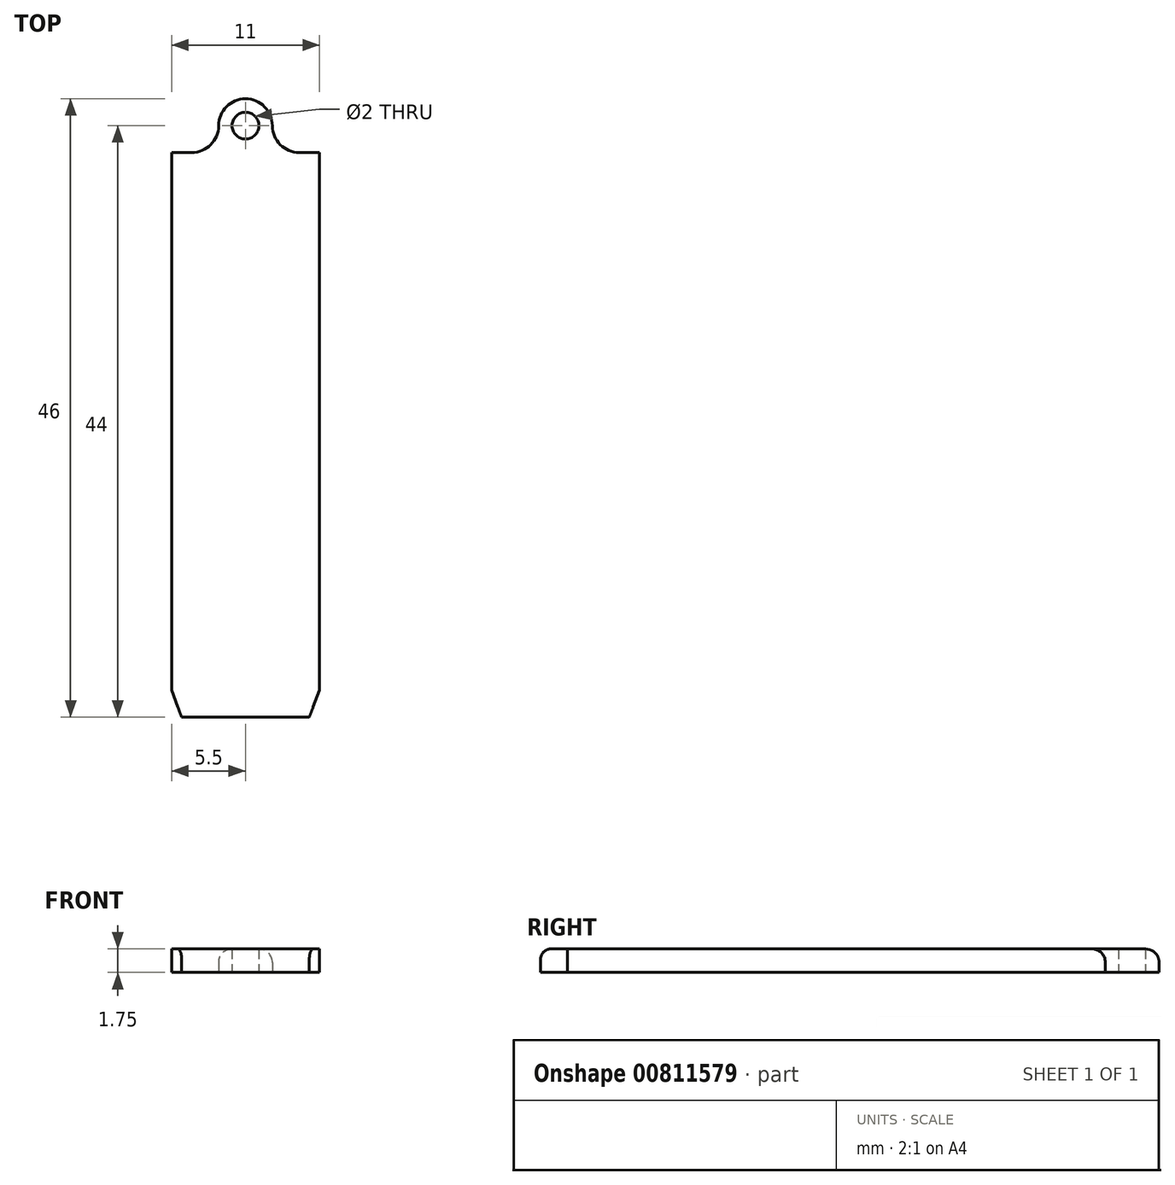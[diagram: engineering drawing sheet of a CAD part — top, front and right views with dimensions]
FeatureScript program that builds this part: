
annotation { "Feature Type Name" : "Feature", "Feature Type Description" : "" }
export const myFeature = defineFeature(function(context is Context, id is Id, definition is map)
    precondition{}
    {
        {
            var Q0;
            Q0=qCreatedBy(makeId("Top.planeOp"),FACE);
            var sketch = newSketch(context, id + "F0", { "sketchPlane" : qUnion([Q0])});
            skLineSegment(sketch, "E0.top", {"start": v(5.5, -21) * mm, "end": v(-5.5, -21) * mm});
            skLineSegment(sketch, "E0.left", {"start": v(5.5, 21) * mm, "end": v(5.5, -21) * mm});
            skLineSegment(sketch, "E0.right", {"start": v(-5.5, 21) * mm, "end": v(-5.5, -21) * mm});
            skPoint(sketch, "E0.middle", {"position": v(0, 0) * mm});
            skLineSegment(sketch, "E1", {"start": v(-2, 23) * mm, "end": v(-2, 23) * mm});
            skLineSegment(sketch, "E2", {"start": v(0, 25) * mm, "end": v(0, 25) * mm});
            skLineSegment(sketch, "E3", {"start": v(2, 23) * mm, "end": v(2, 23) * mm});
            skCircle(sketch, "E4", {"center": v(0, 23) * mm, "radius": 1 * mm});
            skPoint(sketch, "E4.centerSnap0", {"position": v(0, 25) * mm});
            skPoint(sketch, "E4.centerSnap1", {"position": v(-2, 23) * mm});
            skPoint(sketch, "E5.visualSharp", {"position": v(-2, 25) * mm});
            skArc(sketch, "E5.filletArc", {"start": v(0, 25) * mm, "mid": v(-1.41, 24.41) * mm, "end": v(-2, 23) * mm});
            skPoint(sketch, "E6.visualSharp", {"position": v(2, 25) * mm});
            skArc(sketch, "E6.filletArc", {"start": v(2, 23) * mm, "mid": v(1.41, 24.41) * mm, "end": v(0, 25) * mm});
            skLineSegment(sketch, "E7", {"start": v(-5.5, 21) * mm, "end": v(-4, 21) * mm});
            skLineSegment(sketch, "E8", {"start": v(4, 21) * mm, "end": v(5.5, 21) * mm});
            skPoint(sketch, "E9.visualSharp", {"position": v(-2, 21) * mm});
            skArc(sketch, "E9.filletArc", {"start": v(-4, 21) * mm, "mid": v(-2.59, 21.59) * mm, "end": v(-2, 23) * mm});
            skPoint(sketch, "E10.visualSharp", {"position": v(2, 21) * mm});
            skArc(sketch, "E10.filletArc", {"start": v(2, 23) * mm, "mid": v(2.59, 21.59) * mm, "end": v(4, 21) * mm});
            skSolve(sketch);
        }
        {
            var Q0;
            Q0 = qSketchRegion(id + "F0", true);
            extrude(context, id + "F1", {"entities" : qUnion([Q0]), "depth" : 1.75 * mm, "offsetDistance" : 25 * mm});
        }
        {
            var Q0;
            Q0=makeQuery(id+"F1.opExtrude","CAP_EDGE",EDGE,{"disambiguationData":[OSD([sQuery(id+"F0.wireOp",EDGE,"E9.filletArc")])],"isStart":false});
            fillet(context, id + "F2", {"entities" : qUnion([Q0]), "radius" : 1 * mm, "tangentPropagation" : true, "allowEdgeOverflow" : false});
        }
        {
            var Q0;
            Q0=makeQuery(id+"F1.opExtrude","CAP_FACE",FACE,{"disambiguationData":[OSD([sQuery(id+"F0.wireOp",EDGE,"E0.top"),sQuery(id+"F0.wireOp",EDGE,"E0.left"),sQuery(id+"F0.wireOp",EDGE,"E0.right"),sQuery(id+"F0.wireOp",EDGE,"E4"),sQuery(id+"F0.wireOp",EDGE,"E5.filletArc"),sQuery(id+"F0.wireOp",EDGE,"E6.filletArc"),sQuery(id+"F0.wireOp",EDGE,"E7"),sQuery(id+"F0.wireOp",EDGE,"E8"),sQuery(id+"F0.wireOp",EDGE,"E9.filletArc"),sQuery(id+"F0.wireOp",EDGE,"E10.filletArc")])],"isStart":false});
            var sketch = newSketch(context, id + "F3", { "sketchPlane" : qUnion([Q0])});
            skLineSegment(sketch, "E11", {"start": v(-4.75, -21) * mm, "end": v(-5.5, -19) * mm});
            skLineSegment(sketch, "E12", {"start": v(5.5, -19) * mm, "end": v(4.75, -21) * mm});
            skSolve(sketch);
        }
        {
            var Q0;
            {var subQ0=sQuery(id+"F3.wireOp",EDGE,"E11");Q0=makeQuery(id+"F3.imprint","IMPRINT",FACE,{"disambiguationData":[TD([[makeQuery(id+"F3.imprint","IMPRINT",EDGE,{"derivedFrom":subQ0}),1.0]])]});}
            var Q1;
            {var subQ0=sQuery(id+"F3.wireOp",EDGE,"E12");Q1=makeQuery(id+"F3.imprint","IMPRINT",FACE,{"disambiguationData":[TD([[makeQuery(id+"F3.imprint","IMPRINT",EDGE,{"derivedFrom":subQ0}),1.0]])]});}
            extrude(context, id + "F4", {"entities" : qUnion([Q0, Q1]), "operationType" : NewBodyOperationType.REMOVE, "oppositeDirection" : true, "depth" : 25 * mm, "offsetDistance" : 25 * mm});
        }
        {
            var Q0;
            Q0=makeQuery(id+"F4.boolean.opBoolean","COPY",EDGE,{"derivedFrom":makeQuery(id+"F4.opExtrude","CAP_EDGE",EDGE,{"disambiguationData":[OSD([sQuery(id+"F3.wireOp",EDGE,"E11")])],"isStart":true})});
            var Q1;
            Q1=makeQuery(id+"F1.opExtrude","CAP_EDGE",EDGE,{"disambiguationData":[OSD([sQuery(id+"F0.wireOp",EDGE,"E0.top")])],"isStart":false});
            var Q2;
            Q2=makeQuery(id+"F4.boolean.opBoolean","COPY",EDGE,{"derivedFrom":makeQuery(id+"F4.opExtrude","CAP_EDGE",EDGE,{"disambiguationData":[OSD([sQuery(id+"F3.wireOp",EDGE,"E12")])],"isStart":true})});
            var Q3;
            Q3=makeQuery(id+"F4.boolean.opBoolean","COPY",EDGE,{"derivedFrom":makeQuery(id+"F4.opExtrude","SWEPT_EDGE",EDGE,{"disambiguationData":[OSD([sQuery(id+"F0.wireOp",EDGE,"E0.top"),sQuery(id+"F3.wireOp",EDGE,"E11")])]})});
            var Q4;
            Q4=makeQuery(id+"F4.boolean.opBoolean","COPY",EDGE,{"derivedFrom":makeQuery(id+"F4.opExtrude","SWEPT_EDGE",EDGE,{"disambiguationData":[OSD([sQuery(id+"F0.wireOp",EDGE,"E0.top"),sQuery(id+"F3.wireOp",EDGE,"E12")])]})});
            fillet(context, id + "F5", {"entities" : qUnion([Q0, Q1, Q2, Q3, Q4]), "radius" : .75 * mm, "tangentPropagation" : true, "allowEdgeOverflow" : false});
        }
    });
